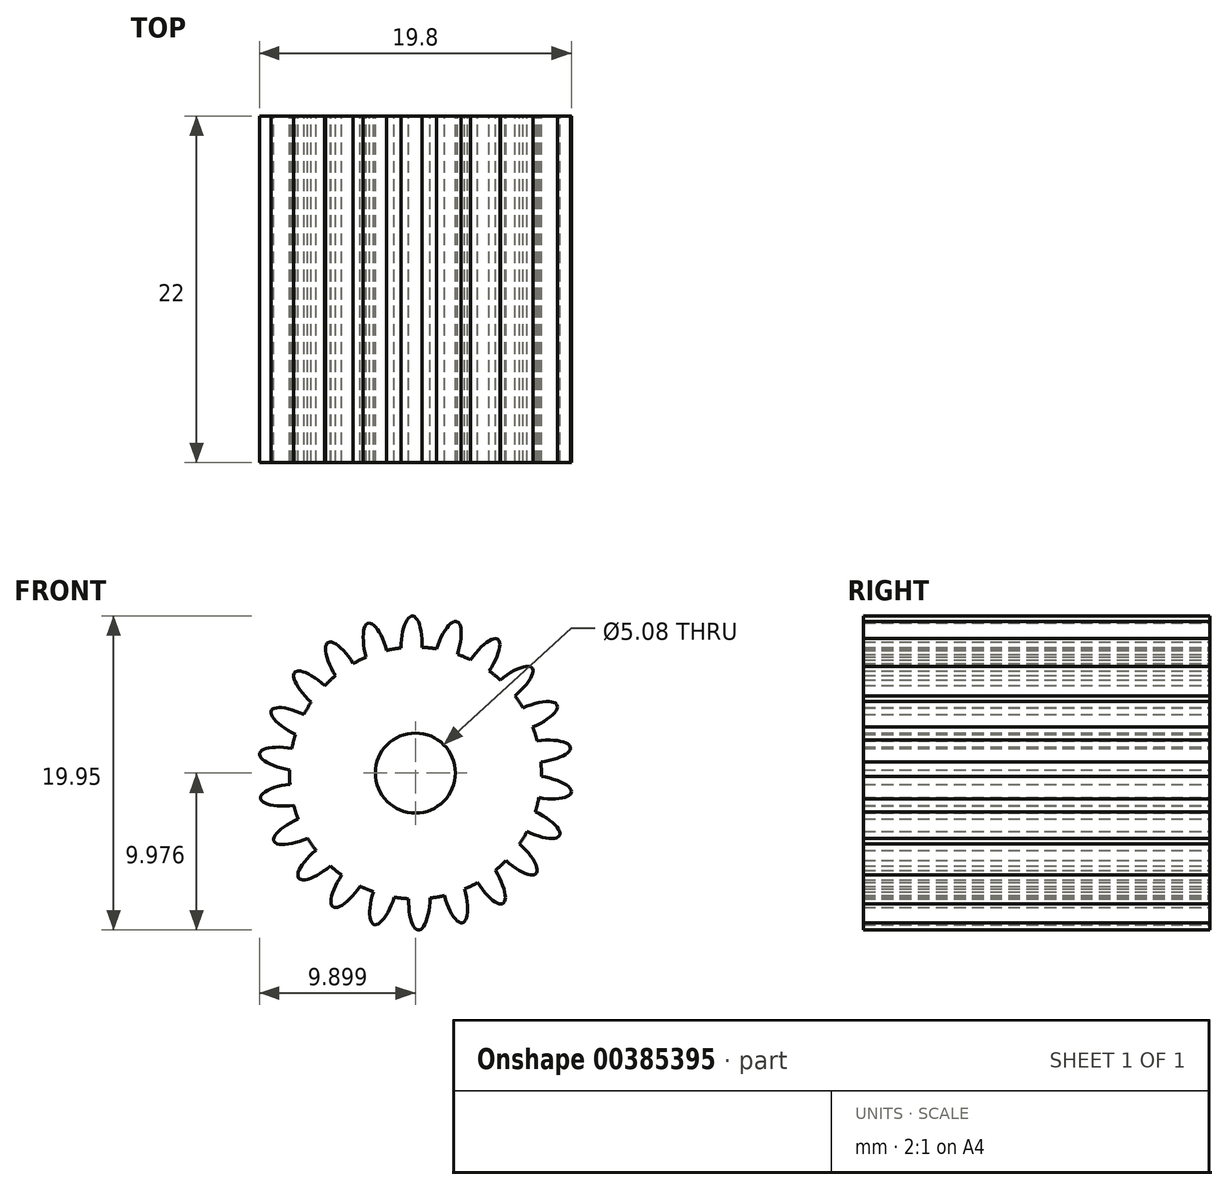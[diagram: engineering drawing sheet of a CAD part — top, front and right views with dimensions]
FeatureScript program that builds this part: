
annotation { "Feature Type Name" : "Feature", "Feature Type Description" : "" }
export const myFeature = defineFeature(function(context is Context, id is Id, definition is map)
    precondition{}
    {
        {
            var Q0;
            Q0=qCreatedBy(makeId("Front.planeOp"),FACE);
            var sketch = newSketch(context, id + "F0", { "sketchPlane" : qUnion([Q0])});
            skCircle(sketch, "E0", {"center": v(0.02, -0.28) * mm, "radius": 8 * mm});
            skLineSegment(sketch, "E1", {"start": v(0.02, -0.28) * mm, "end": v(-1.14, 7.63) * mm});
            skLineSegment(sketch, "E2", {"start": v(0.02, -0.28) * mm, "end": v(0.12, 7.72) * mm});
            skEllipticalArc(sketch, "E3.38.0", {});
            skCircle(sketch, "E4", {"center": v(0.02, -0.28) * mm, "radius": 2.54 * mm});
            skEllipticalArc(sketch, "E5.1.0", {});
            skEllipticalArc(sketch, "E5.2.0", {});
            skEllipticalArc(sketch, "E5.3.0", {});
            skEllipticalArc(sketch, "E5.4.0", {});
            skEllipticalArc(sketch, "E5.5.0", {});
            skEllipticalArc(sketch, "E5.6.0", {});
            skEllipticalArc(sketch, "E5.7.0", {});
            skEllipticalArc(sketch, "E5.8.0", {});
            skEllipticalArc(sketch, "E5.9.0", {});
            skEllipticalArc(sketch, "E5.10.0", {});
            skEllipticalArc(sketch, "E5.11.0", {});
            skEllipticalArc(sketch, "E5.12.0", {});
            skEllipticalArc(sketch, "E5.13.0", {});
            skEllipticalArc(sketch, "E5.14.0", {});
            skEllipticalArc(sketch, "E5.15.0", {});
            skEllipticalArc(sketch, "E5.16.0", {});
            skEllipticalArc(sketch, "E5.17.0", {});
            skEllipticalArc(sketch, "E5.18.0", {});
            skEllipticalArc(sketch, "E5.19.0", {});
            skEllipticalArc(sketch, "E5.20.0", {});
            skEllipticalArc(sketch, "E5.21.0", {});
            const initialGuessF0  = {"E3.38.0": [0.0020338387929103824, 0.007457887595116231, -0.3090169943749474, -0.9510565162951536, 0.0019768298493211675, 0.0006797314705727096, 1.5766588321977384, 4.747653305813112], "E5.1.0": [-0.0002289802865234425, 0.007711952923515431, -0.02855605079369622, -0.9995921928281893, 0.0019768298493211675, 0.0006797314705727096, 1.5766588321977386, 4.747653305813111], "E5.2.0": [-0.0024717177683756864, 0.007318217016035061, 0.25421833419348694, -0.9671468547019572, 0.0019768298493211675, 0.0006797314705727096, 1.5766588321977386, 4.747653305813111], "E5.3.0": [-0.00451268039994006, 0.006308578014261577, 0.5163974616389619, -0.856349030251589, 0.0019768298493211675, 0.0006797314705727096, 1.5766588321977386, 4.747653305813111], "E5.4.0": [-0.00618652152687936, 0.004764830865564319, 0.7367411378764049, -0.6761749002740194, 0.0019768298493211675, 0.0006797314705727096, 1.5766588321977386, 4.747653305813111], "E5.5.0": [-0.0073576364958054434, 0.002812040782912937, 0.8973984286913584, -0.4412211012432212, 0.0019768298493211675, 0.0006797314705727096, 1.5766588321977386, 4.747653305813111], "E5.6.0": [-0.007931148536824821, 0.0006084112051140463, 0.9853538358476931, -0.1705221926326239, 0.0019768298493211675, 0.0006797314705727096, 1.5766588321977386, 4.747653305813111], "E5.7.0": [-0.007860595115181541, -0.0016675329049288083, 0.9934817353485503, 0.11399140989054057, 0.0019768298493211675, 0.0006797314705727096, 1.5766588321977386, 4.747653305813111], "E5.8.0": [-0.0071516920494997865, -0.0038314080909807543, 0.9211236531148501, 0.38927010631739145, 0.0019768298493211675, 0.0006797314705727096, 1.5766588321977386, 4.747653305813111], "E5.9.0": [-0.00586187045015223, -0.005707910054529112, 0.7741416106390826, 0.6330124538088703, 0.0019768298493211675, 0.0006797314705727096, 1.5766588321977386, 4.747653305813111], "E5.10.0": [-0.00409562399225359, -0.00714501576647408, 0.5644432188667692, 0.825471896962774, 0.0019768298493211675, 0.0006797314705727096, 1.5766588321977386, 4.747653305813111], "E5.11.0": [-0.001996043459550679, -0.008026299468830633, 0.30901699437494795, 0.9510565162951534, 0.0019768298493211675, 0.0006797314705727096, 1.5766588321977386, 4.747653305813111], "E5.12.0": [0.00026677561988314787, -0.008280364797229833, 0.028556050793696552, 0.9995921928281893, 0.0019768298493211675, 0.0006797314705727096, 1.5766588321977386, 4.747653305813111], "E5.13.0": [0.0025095131017353945, -0.007886628889749463, -0.25421833419348694, 0.9671468547019572, 0.0019768298493211675, 0.0006797314705727096, 1.5766588321977386, 4.747653305813111], "E5.14.0": [0.004550475733299767, -0.00687698988797598, -0.5163974616389618, 0.856349030251589, 0.0019768298493211675, 0.0006797314705727096, 1.5766588321977386, 4.747653305813111], "E5.15.0": [0.006224316860239064, -0.005333242739278726, -0.7367411378764044, 0.67617490027402, 0.0019768298493211675, 0.0006797314705727096, 1.5766588321977386, 4.747653305813111], "E5.16.0": [0.007395431829165151, -0.0033804526566273397, -0.8973984286913584, 0.44122110124322134, 0.0019768298493211675, 0.0006797314705727096, 1.5766588321977386, 4.747653305813111], "E5.17.0": [0.00796894387018453, -0.001176823078828449, -0.9853538358476931, 0.170522192632624, 0.0019768298493211675, 0.0006797314705727096, 1.5766588321977386, 4.747653305813111], "E5.18.0": [0.00789839044854125, 0.0010991210312144043, -0.9934817353485503, -0.11399140989054024, 0.0019768298493211675, 0.0006797314705727096, 1.5766588321977386, 4.747653305813111], "E5.19.0": [0.007189487382859497, 0.0032629962172663492, -0.9211236531148503, -0.3892701063173909, 0.0019768298493211675, 0.0006797314705727096, 1.5766588321977386, 4.747653305813111], "E5.20.0": [0.005899665783511935, 0.0051394981808147115, -0.7741416106390825, -0.6330124538088706, 0.0019768298493211675, 0.0006797314705727096, 1.5766588321977386, 4.747653305813111], "E5.21.0": [0.004133419325613299, 0.006576603892759677, -0.5644432188667692, -0.825471896962774, 0.0019768298493211675, 0.0006797314705727096, 1.5766588321977386, 4.747653305813111]};
            skSetInitialGuess(sketch, initialGuessF0);
            skSolve(sketch);
        }
        {
            var Q0;
            Q0 = qSketchRegion(id + "F0", true);
            extrude(context, id + "F1", {"entities" : qUnion([Q0]), "depth" : 22 * mm});
        }
    });
